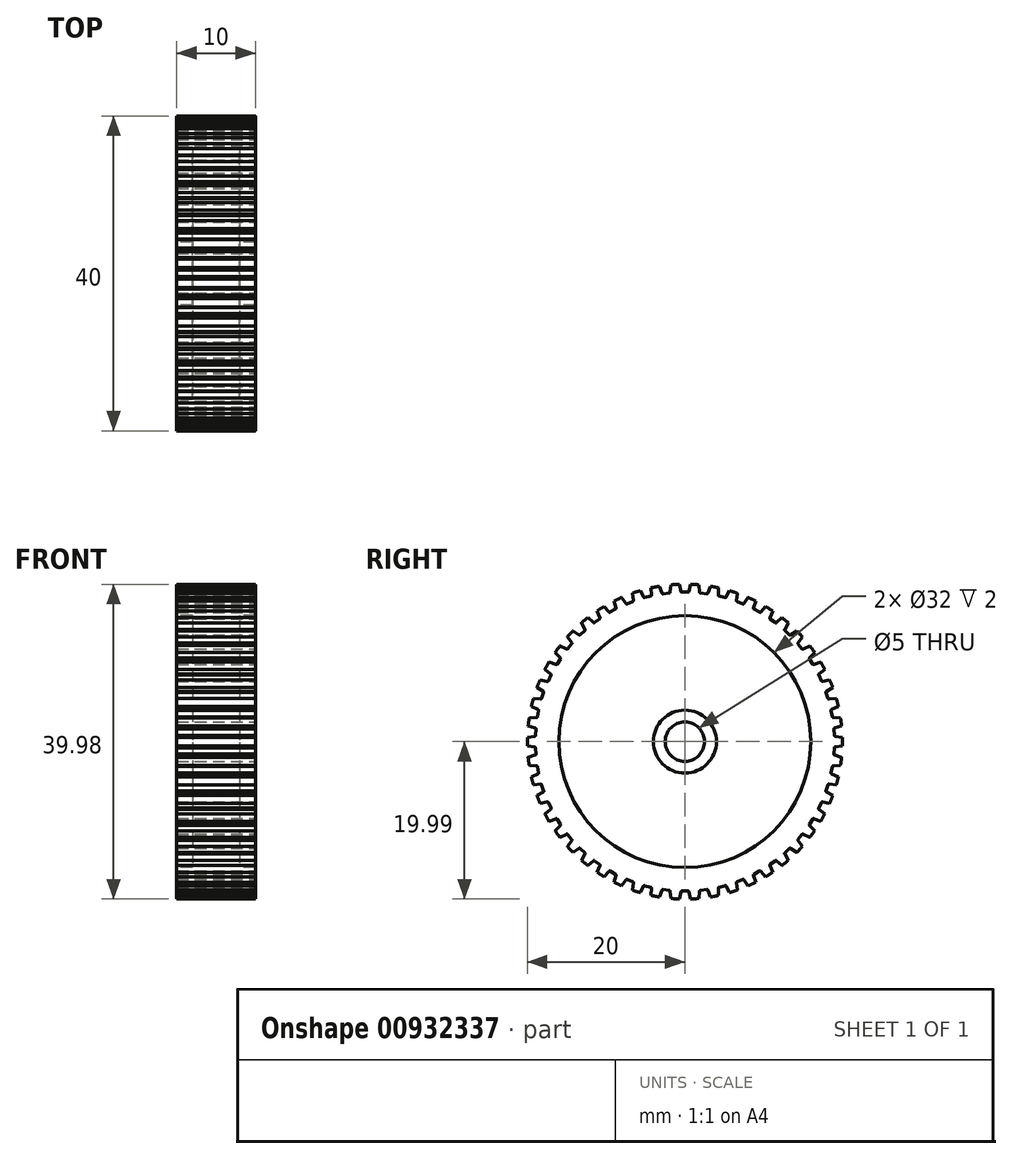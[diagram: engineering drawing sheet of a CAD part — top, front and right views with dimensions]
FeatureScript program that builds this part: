
annotation { "Feature Type Name" : "Feature", "Feature Type Description" : "" }
export const myFeature = defineFeature(function(context is Context, id is Id, definition is map)
    precondition{}
    {
        {
            var Q0;
            Q0=qCreatedBy(makeId("Front.planeOp"),FACE);
            var sketch = newSketch(context, id + "F0", { "sketchPlane" : qUnion([Q0])});
            skLineSegment(sketch, "E0.bottom", {"start": v(0, 0) * mm, "end": v(-5, 0) * mm});
            skLineSegment(sketch, "E0.top", {"start": v(0, 20) * mm, "end": v(-5, 20) * mm});
            skLineSegment(sketch, "E0.left", {"start": v(0, 0) * mm, "end": v(0, 20) * mm});
            skLineSegment(sketch, "E0.right", {"start": v(-5, 0) * mm, "end": v(-5, 4) * mm});
            skLineSegment(sketch, "E1", {"start": v(-5, 16) * mm, "end": v(-5, 20) * mm});
            skLineSegment(sketch, "E2.bottom", {"start": v(-5, 4) * mm, "end": v(-3, 4) * mm});
            skLineSegment(sketch, "E2.top", {"start": v(-5, 16) * mm, "end": v(-3, 16) * mm});
            skLineSegment(sketch, "E2.right", {"start": v(-3, 4) * mm, "end": v(-3, 16) * mm});
            skLineSegment(sketch, "E3.MirrorCS", {"start": v(0, 20) * mm, "end": v(5, 20) * mm});
            skLineSegment(sketch, "E4.MirrorCS", {"start": v(5, 16) * mm, "end": v(5, 20) * mm});
            skLineSegment(sketch, "E5.MirrorCS", {"start": v(3, 4) * mm, "end": v(3, 16) * mm});
            skLineSegment(sketch, "E6.MirrorCS", {"start": v(5, 16) * mm, "end": v(3, 16) * mm});
            skLineSegment(sketch, "E7.MirrorCS", {"start": v(5, 4) * mm, "end": v(3, 4) * mm});
            skLineSegment(sketch, "E8.MirrorCS", {"start": v(5, 0) * mm, "end": v(5, 4) * mm});
            skLineSegment(sketch, "E9.MirrorCS", {"start": v(0, 0) * mm, "end": v(5, 0) * mm});
            skSolve(sketch);
        }
        {
            var Q0;
            Q0=makeQuery(id+"F0.imprint","IMPRINT",FACE,{"disambiguationData":[TD([[makeQuery(id+"F0.imprint","IMPRINT",EDGE,{"derivedFrom":sQuery(id+"F0.wireOp",EDGE,"E0.left")}),-1.0]])]});
            var Q1;
            Q1=makeQuery(id+"F0.imprint","IMPRINT",FACE,{"disambiguationData":[TD([[makeQuery(id+"F0.imprint","IMPRINT",EDGE,{"derivedFrom":sQuery(id+"F0.wireOp",EDGE,"E0.bottom")}),-1.0]])]});
            var Q2;
            Q2=sQuery(id+"F0.wireOp",EDGE,"E9.MirrorCS");
            revolve(context, id + "F1", {"surfaceOperationType" : NewSurfaceOperationType.NEW, "entities" : qUnion([Q0, Q1]), "axis" : qUnion([Q2]), "revolveType" : RevolveType.FULL});
        }
        {
            var Q0;
            Q0=qCreatedBy(makeId("Right.planeOp"),FACE);
            var sketch = newSketch(context, id + "F2", { "sketchPlane" : qUnion([Q0])});
            skLineSegment(sketch, "E10", {"start": v(0, 0) * mm, "end": v(0, 20) * mm});
            skLineSegment(sketch, "E11", {"start": v(0.72, 19.99) * mm, "end": v(0.52, 19.08) * mm});
            skLineSegment(sketch, "E12.MirrorCS", {"start": v(-0.72, 19.99) * mm, "end": v(-0.52, 19.08) * mm});
            skLineSegment(sketch, "E13", {"start": v(-0.4, 18.99) * mm, "end": v(0.4, 18.99) * mm});
            skPoint(sketch, "E14.visualSharp", {"position": v(0.5, 18.99) * mm});
            skArc(sketch, "E14.filletArc", {"start": v(0.4, 18.99) * mm, "mid": v(0.48, 19.01) * mm, "end": v(0.52, 19.08) * mm});
            skPoint(sketch, "E15.visualSharp", {"position": v(-0.5, 18.99) * mm});
            skArc(sketch, "E15.filletArc", {"start": v(-0.52, 19.08) * mm, "mid": v(-0.48, 19.01) * mm, "end": v(-0.4, 18.99) * mm});
            skLineSegment(sketch, "E16", {"start": v(0.72, 19.99) * mm, "end": v(0, 20) * mm});
            skLineSegment(sketch, "E17", {"start": v(-0.72, 19.99) * mm, "end": v(0, 20) * mm});
            skSolve(sketch);
        }
        {
            var Q0;
            {var subQ4=sQuery(id+"F2.wireOp",EDGE,"E11");Q0=makeQuery(id+"F2.imprint","IMPRINT",FACE,{"disambiguationData":[TD([[makeQuery(id+"F2.imprint","IMPRINT",EDGE,{"derivedFrom":subQ4}),-1.0]])]});}
            var Q1;
            {var subQ4=sQuery(id+"F2.wireOp",EDGE,"E12.MirrorCS");Q1=makeQuery(id+"F2.imprint","IMPRINT",FACE,{"disambiguationData":[TD([[makeQuery(id+"F2.imprint","IMPRINT",EDGE,{"derivedFrom":subQ4}),1.0]])]});}
            extrude(context, id + "F3", {"entities" : qUnion([Q0, Q1]), "operationType" : NewBodyOperationType.REMOVE, "endBound" : BoundingType.SYMMETRIC, "oppositeDirection" : true, "depth" : 25 * mm, "offsetDistance" : 25 * mm});
        }
        {
            var Q0;
            Q0=makeQuery(id+"F3.boolean.opBoolean","COPY",FACE,{"derivedFrom":makeQuery(id+"F3.opExtrude","SWEPT_FACE",FACE,{"disambiguationData":[OSD([sQuery(id+"F2.wireOp",EDGE,"E11")])]})});
            var Q1;
            Q1=makeQuery(id+"F3.boolean.opBoolean","COPY",FACE,{"derivedFrom":makeQuery(id+"F3.opExtrude","SWEPT_FACE",FACE,{"disambiguationData":[OSD([sQuery(id+"F2.wireOp",EDGE,"E14.filletArc")])]})});
            var Q2;
            Q2=makeQuery(id+"F3.boolean.opBoolean","COPY",FACE,{"derivedFrom":makeQuery(id+"F3.opExtrude","SWEPT_FACE",FACE,{"disambiguationData":[OSD([sQuery(id+"F2.wireOp",EDGE,"E13")])]})});
            var Q3;
            Q3=makeQuery(id+"F3.boolean.opBoolean","COPY",FACE,{"derivedFrom":makeQuery(id+"F3.opExtrude","SWEPT_FACE",FACE,{"disambiguationData":[OSD([sQuery(id+"F2.wireOp",EDGE,"E15.filletArc")])]})});
            var Q4;
            Q4=makeQuery(id+"F3.boolean.opBoolean","COPY",FACE,{"derivedFrom":makeQuery(id+"F3.opExtrude","SWEPT_FACE",FACE,{"disambiguationData":[OSD([sQuery(id+"F2.wireOp",EDGE,"E12.MirrorCS")])]})});
            var Q5;
            Q5=makeQuery(id+"F1.opRevolve","SWEPT_FACE",FACE,{"disambiguationData":[OSD([sQuery(id+"F0.wireOp",EDGE,"E0.top"),sQuery(id+"F0.wireOp",EDGE,"E3.MirrorCS")])]});
            circularPattern(context, id + "F4", {"patternType" : PatternType.FACE, "faces" : qUnion([Q0, Q1, Q2, Q3, Q4]), "axis" : qUnion([Q5]), "angle" : 360 * degree, "instanceCount" : 50, "equalSpace" : true});
        }
        {
            var Q0;
            Q0=makeQuery(id+"F1.opRevolve","SWEPT_FACE",FACE,{"disambiguationData":[OSD([sQuery(id+"F0.wireOp",EDGE,"E8.MirrorCS")])]});
            var sketch = newSketch(context, id + "F5", { "sketchPlane" : qUnion([Q0])});
            skCircle(sketch, "E18", {"center": v(0, 0) * mm, "radius": 2.5 * mm});
            skSolve(sketch);
        }
        {
            var Q0;
            Q0=makeQuery(id+"F5.imprint","IMPRINT",FACE,{"disambiguationData":[TD([[makeQuery(id+"F5.imprint","IMPRINT",EDGE,{"derivedFrom":sQuery(id+"F5.wireOp",EDGE,"E18")}),1.0]])]});
            extrude(context, id + "F6", {"entities" : qUnion([Q0]), "operationType" : NewBodyOperationType.REMOVE, "oppositeDirection" : true, "depth" : 25 * mm, "offsetDistance" : 25 * mm});
        }
    });
